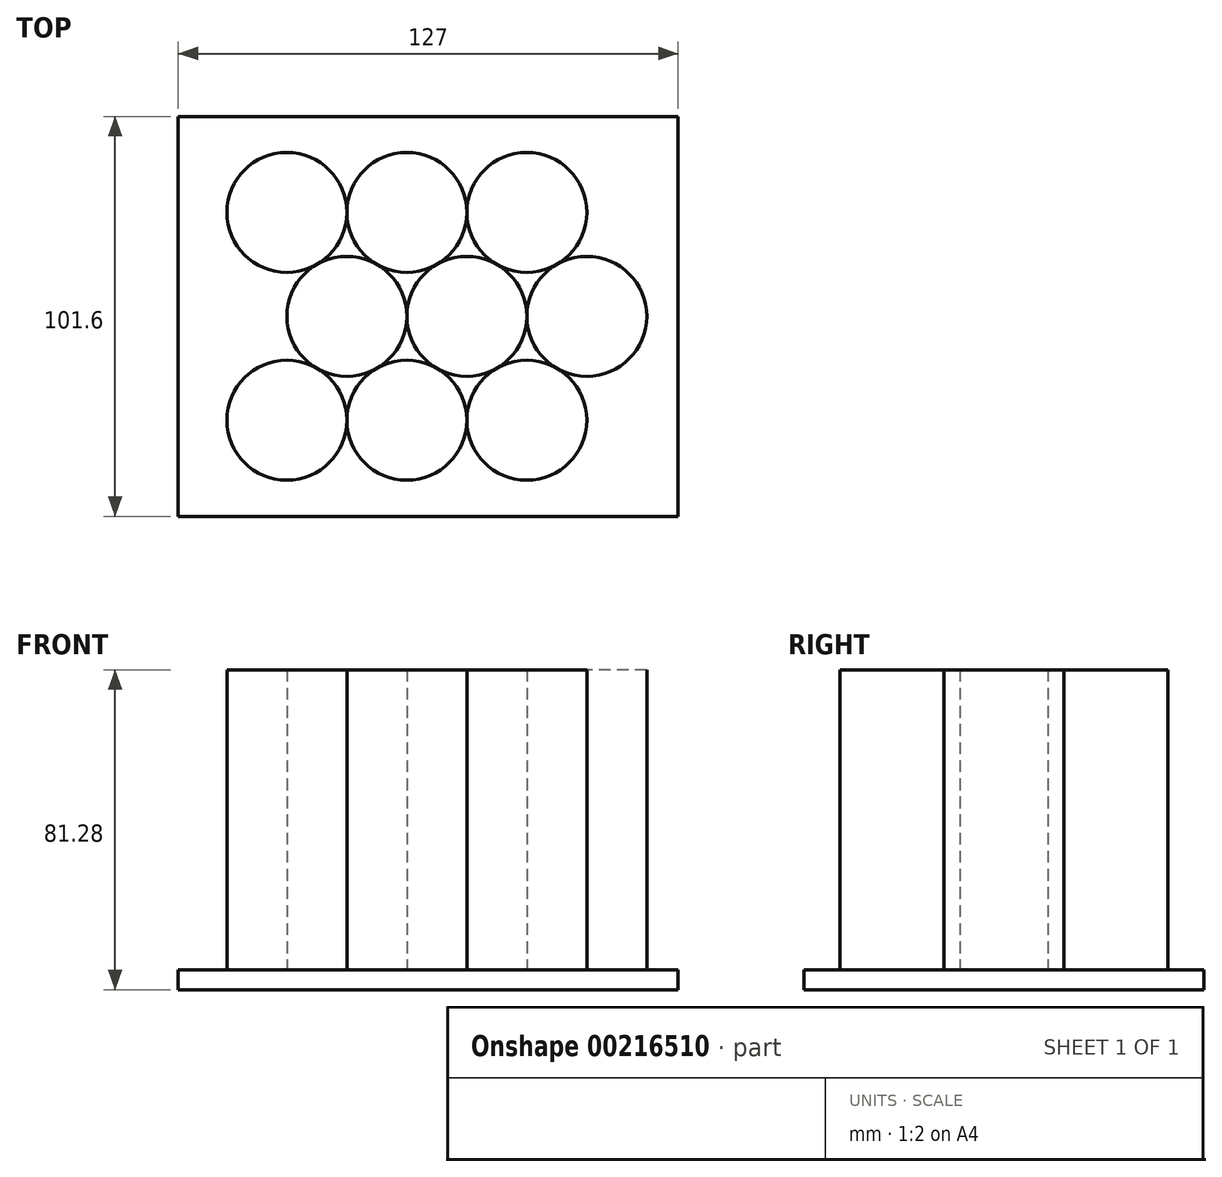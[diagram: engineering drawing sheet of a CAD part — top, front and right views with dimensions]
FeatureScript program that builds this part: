
annotation { "Feature Type Name" : "Feature", "Feature Type Description" : "" }
export const myFeature = defineFeature(function(context is Context, id is Id, definition is map)
    precondition{}
    {
        {
            var Q0;
            Q0=qCreatedBy(makeId("Top.planeOp"),FACE);
            var sketch = newSketch(context, id + "F0", { "sketchPlane" : qUnion([Q0])});
            skCircle(sketch, "E0", {"center": v(-35.9, 26.4) * mm, "radius": 15.24 * mm});
            skCircle(sketch, "E1", {"center": v(-5.42, 26.4) * mm, "radius": 15.24 * mm});
            skCircle(sketch, "E2", {"center": v(25.06, 26.4) * mm, "radius": 15.24 * mm});
            skLineSegment(sketch, "E3", {"start": v(-35.9, 26.4) * mm, "end": v(35.93, 26.4) * mm, "construction": true});
            skCircle(sketch, "E4", {"center": v(-20.66, 0) * mm, "radius": 15.24 * mm});
            skCircle(sketch, "E5", {"center": v(9.82, 0) * mm, "radius": 15.24 * mm});
            skCircle(sketch, "E6", {"center": v(40.3, 0) * mm, "radius": 15.24 * mm});
            skLineSegment(sketch, "E7", {"start": v(-20.66, 0) * mm, "end": v(6.67, 0) * mm, "construction": true});
            skCircle(sketch, "E8", {"center": v(-35.9, -26.4) * mm, "radius": 15.24 * mm});
            skCircle(sketch, "E9", {"center": v(-5.42, -26.4) * mm, "radius": 15.24 * mm});
            skCircle(sketch, "E10", {"center": v(25.06, -26.4) * mm, "radius": 15.24 * mm});
            skLineSegment(sketch, "E11", {"start": v(-35.9, -26.4) * mm, "end": v(51.13, -26.4) * mm, "construction": true});
            skSolve(sketch);
        }
        {
            var Q0;
            {var subQ0=sQuery(id+"F0.wireOp",EDGE,"E0");var subQ1=makeQuery(id+"F0.imprint","INTERSECT",VERTEX,{"derivedFrom":[subQ0,sQuery(id+"F0.wireOp",EDGE,"E1")]});Q0=makeQuery(id+"F0.imprint","IMPRINT",FACE,{"disambiguationData":[TD([[makeQuery(id+"F0.imprint","IMPRINT",EDGE,{"disambiguationData":[TD([[subQ1,-1.0]])],"derivedFrom":subQ0}),1.0]])]});}
            var Q1;
            {var subQ0=sQuery(id+"F0.wireOp",EDGE,"E1");var subQ1=makeQuery(id+"F0.imprint","INTERSECT",VERTEX,{"derivedFrom":[sQuery(id+"F0.wireOp",EDGE,"E0"),subQ0]});Q1=makeQuery(id+"F0.imprint","IMPRINT",FACE,{"disambiguationData":[TD([[makeQuery(id+"F0.imprint","IMPRINT",EDGE,{"disambiguationData":[TD([[subQ1,1.0]])],"derivedFrom":subQ0}),1.0]])]});}
            var Q2;
            {var subQ0=sQuery(id+"F0.wireOp",EDGE,"E2");var subQ1=makeQuery(id+"F0.imprint","INTERSECT",VERTEX,{"derivedFrom":[sQuery(id+"F0.wireOp",EDGE,"E1"),subQ0]});Q2=makeQuery(id+"F0.imprint","IMPRINT",FACE,{"disambiguationData":[TD([[makeQuery(id+"F0.imprint","IMPRINT",EDGE,{"disambiguationData":[TD([[subQ1,-1.0]])],"derivedFrom":subQ0}),1.0]])]});}
            var Q3;
            {var subQ0=sQuery(id+"F0.wireOp",EDGE,"E6");var subQ1=makeQuery(id+"F0.imprint","INTERSECT",VERTEX,{"derivedFrom":[sQuery(id+"F0.wireOp",EDGE,"E2"),subQ0]});Q3=makeQuery(id+"F0.imprint","IMPRINT",FACE,{"disambiguationData":[TD([[makeQuery(id+"F0.imprint","IMPRINT",EDGE,{"disambiguationData":[TD([[subQ1,-1.0]])],"derivedFrom":subQ0}),1.0]])]});}
            var Q4;
            {var subQ0=sQuery(id+"F0.wireOp",EDGE,"E5");var subQ4=makeQuery(id+"F0.imprint","INTERSECT",VERTEX,{"derivedFrom":[sQuery(id+"F0.wireOp",EDGE,"E2"),subQ0]});Q4=makeQuery(id+"F0.imprint","IMPRINT",FACE,{"disambiguationData":[TD([[makeQuery(id+"F0.imprint","IMPRINT",EDGE,{"disambiguationData":[TD([[subQ4,1.0]])],"derivedFrom":subQ0}),1.0]])]});}
            var Q5;
            {var subQ0=sQuery(id+"F0.wireOp",EDGE,"E4");var subQ4=makeQuery(id+"F0.imprint","INTERSECT",VERTEX,{"derivedFrom":[sQuery(id+"F0.wireOp",EDGE,"E1"),subQ0]});Q5=makeQuery(id+"F0.imprint","IMPRINT",FACE,{"disambiguationData":[TD([[makeQuery(id+"F0.imprint","IMPRINT",EDGE,{"disambiguationData":[TD([[subQ4,1.0]])],"derivedFrom":subQ0}),1.0]])]});}
            var Q6;
            {var subQ0=sQuery(id+"F0.wireOp",EDGE,"E8");var subQ1=makeQuery(id+"F0.imprint","INTERSECT",VERTEX,{"derivedFrom":[sQuery(id+"F0.wireOp",EDGE,"E4"),subQ0]});Q6=makeQuery(id+"F0.imprint","IMPRINT",FACE,{"disambiguationData":[TD([[makeQuery(id+"F0.imprint","IMPRINT",EDGE,{"disambiguationData":[TD([[subQ1,1.0]])],"derivedFrom":subQ0}),1.0]])]});}
            var Q7;
            {var subQ0=sQuery(id+"F0.wireOp",EDGE,"E9");var subQ1=makeQuery(id+"F0.imprint","INTERSECT",VERTEX,{"derivedFrom":[subQ0,sQuery(id+"F0.wireOp",EDGE,"E10")]});Q7=makeQuery(id+"F0.imprint","IMPRINT",FACE,{"disambiguationData":[TD([[makeQuery(id+"F0.imprint","IMPRINT",EDGE,{"disambiguationData":[TD([[subQ1,-1.0]])],"derivedFrom":subQ0}),1.0]])]});}
            var Q8;
            {var subQ0=sQuery(id+"F0.wireOp",EDGE,"E10");var subQ1=makeQuery(id+"F0.imprint","INTERSECT",VERTEX,{"derivedFrom":[sQuery(id+"F0.wireOp",EDGE,"E6"),subQ0]});Q8=makeQuery(id+"F0.imprint","IMPRINT",FACE,{"disambiguationData":[TD([[makeQuery(id+"F0.imprint","IMPRINT",EDGE,{"disambiguationData":[TD([[subQ1,-1.0]])],"derivedFrom":subQ0}),1.0]])]});}
            var Q9;
            Q9=sQuery(id+"F0.wireOp",EDGE,"E5");
            var Q10;
            Q10=sQuery(id+"F0.wireOp",EDGE,"E0");
            var Q11;
            Q11=sQuery(id+"F0.wireOp",EDGE,"E10");
            var Q12;
            Q12=sQuery(id+"F0.wireOp",EDGE,"E9");
            var Q13;
            Q13=sQuery(id+"F0.wireOp",EDGE,"E8");
            var Q14;
            Q14=sQuery(id+"F0.wireOp",EDGE,"E6");
            var Q15;
            Q15=sQuery(id+"F0.wireOp",EDGE,"E4");
            var Q16;
            Q16=sQuery(id+"F0.wireOp",EDGE,"E2");
            var Q17;
            Q17=sQuery(id+"F0.wireOp",EDGE,"E1");
            extrude(context, id + "F1", {"entities" : qUnion([Q0, Q1, Q2, Q3, Q4, Q5, Q6, Q7, Q8]), "surfaceEntities" : qUnion([Q9, Q10, Q11, Q12, Q13, Q14, Q15, Q16, Q17]), "depth" : 76.2 * mm});
        }
        {
            var Q0;
            Q0=qCreatedBy(makeId("Front.planeOp"),FACE);
            var sketch = newSketch(context, id + "F2", { "sketchPlane" : qUnion([Q0])});
            skLineSegment(sketch, "E12.bottom", {"start": v(63.5, 0) * mm, "end": v(-63.5, 0) * mm});
            skLineSegment(sketch, "E12.top", {"start": v(63.5, -5.08) * mm, "end": v(-63.5, -5.08) * mm});
            skLineSegment(sketch, "E12.left", {"start": v(63.5, 0) * mm, "end": v(63.5, -5.08) * mm});
            skLineSegment(sketch, "E12.right", {"start": v(-63.5, 0) * mm, "end": v(-63.5, -5.08) * mm});
            skSolve(sketch);
        }
        {
            var Q0;
            Q0=makeQuery(id+"F2.imprint","IMPRINT",FACE,{"disambiguationData":[TD([[makeQuery(id+"F2.imprint","IMPRINT",EDGE,{"derivedFrom":sQuery(id+"F2.wireOp",EDGE,"E12.bottom")}),1.0]])]});
            var Q1;
            Q1=sQuery(id+"F2.wireOp",EDGE,"E12.bottom");
            extrude(context, id + "F3", {"entities" : qUnion([Q0]), "surfaceEntities" : qUnion([Q1]), "endBound" : BoundingType.SYMMETRIC, "oppositeDirection" : true, "depth" : 101.6 * mm});
        }
    });
